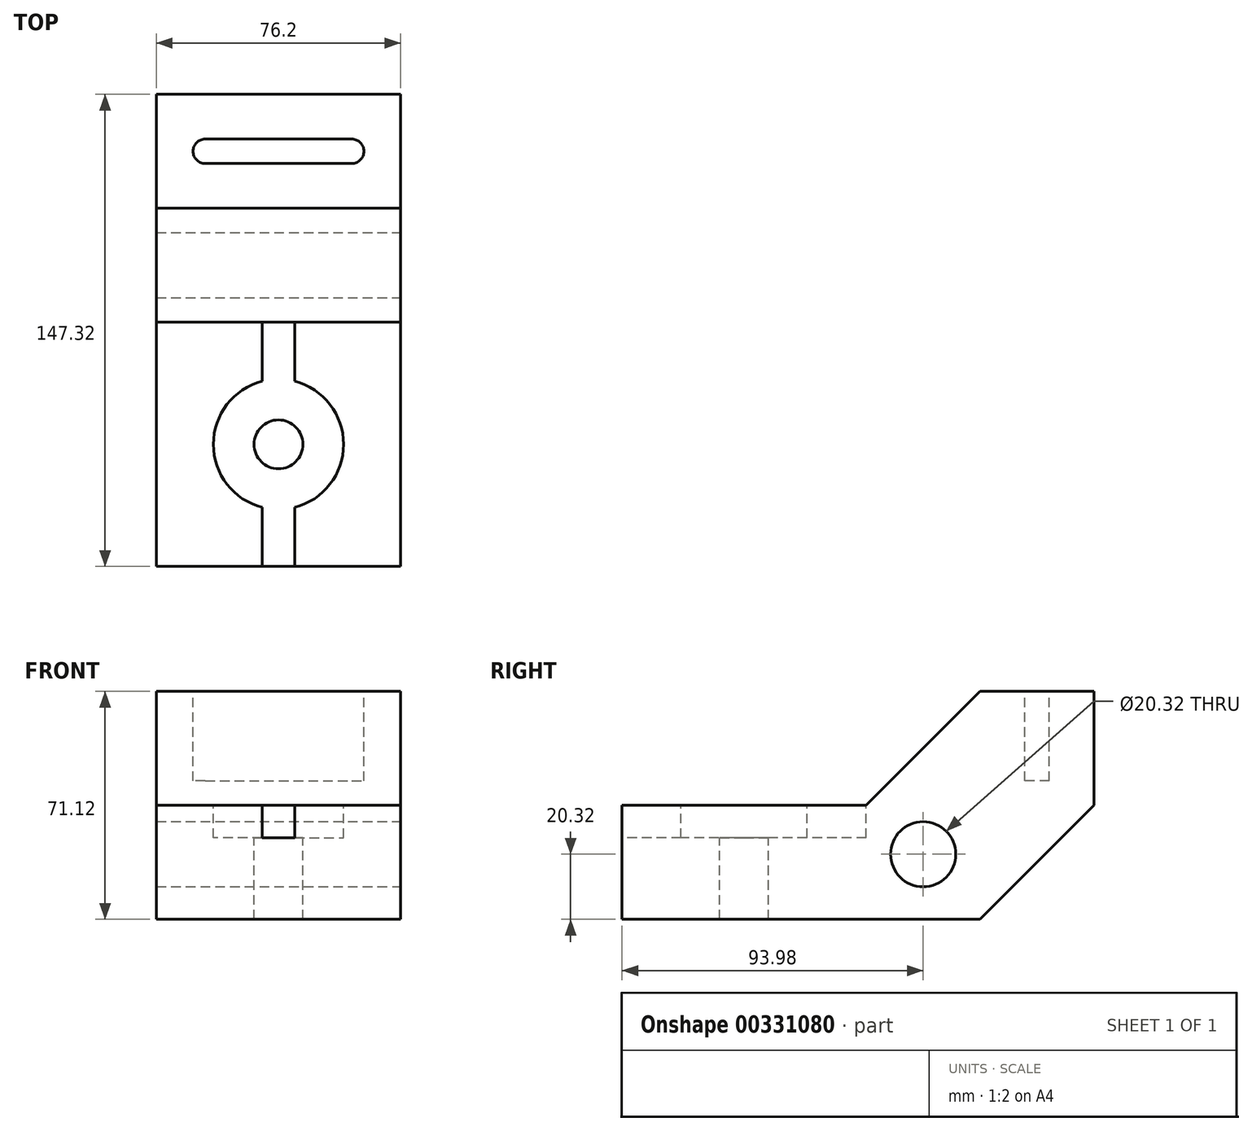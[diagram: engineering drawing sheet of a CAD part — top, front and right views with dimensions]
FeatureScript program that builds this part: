
annotation { "Feature Type Name" : "Feature", "Feature Type Description" : "" }
export const myFeature = defineFeature(function(context is Context, id is Id, definition is map)
    precondition{}
    {
        {
            var Q0;
            Q0=qCreatedBy(makeId("Right.planeOp"),FACE);
            var sketch = newSketch(context, id + "F0", { "sketchPlane" : qUnion([Q0])});
            skLineSegment(sketch, "E0.bottom", {"start": v(-73.66, 0) * mm, "end": v(73.66, 0) * mm});
            skLineSegment(sketch, "E0.top", {"start": v(-73.66, 71.12) * mm, "end": v(73.66, 71.12) * mm});
            skLineSegment(sketch, "E0.left", {"start": v(-73.66, 0) * mm, "end": v(-73.66, 71.12) * mm});
            skLineSegment(sketch, "E0.right", {"start": v(73.66, 0) * mm, "end": v(73.66, 71.12) * mm});
            skSolve(sketch);
        }
        {
            var Q0;
            Q0 = qSketchRegion(id + "F0", true);
            extrude(context, id + "F1", {"entities" : qUnion([Q0]), "endBound" : BoundingType.SYMMETRIC, "depth" : 76.2 * mm});
        }
        {
            var Q0;
            Q0=makeQuery(id+"F1.opExtrude","CAP_FACE",FACE,{"disambiguationData":[OSD([sQuery(id+"F0.wireOp",EDGE,"E0.bottom"),sQuery(id+"F0.wireOp",EDGE,"E0.top"),sQuery(id+"F0.wireOp",EDGE,"E0.left"),sQuery(id+"F0.wireOp",EDGE,"E0.right")])],"isStart":false});
            var sketch = newSketch(context, id + "F2", { "sketchPlane" : qUnion([Q0])});
            skLineSegment(sketch, "E1.0.0", {"start": v(38.1, 71.12) * mm, "end": v(-73.66, 71.12) * mm});
            skLineSegment(sketch, "E1.0.1", {"start": v(-73.66, 71.12) * mm, "end": v(-73.66, 35.56) * mm});
            skLineSegment(sketch, "E1.0.2", {"start": v(38.1, 0) * mm, "end": v(73.66, 0) * mm});
            skLineSegment(sketch, "E1.0.3", {"start": v(73.66, 0) * mm, "end": v(73.66, 35.56) * mm});
            skLineSegment(sketch, "E2", {"start": v(73.66, 35.56) * mm, "end": v(38.1, 0) * mm});
            skLineSegment(sketch, "E3", {"start": v(-73.66, 35.56) * mm, "end": v(2.54, 35.56) * mm});
            skLineSegment(sketch, "E4", {"start": v(2.54, 35.56) * mm, "end": v(38.1, 71.12) * mm});
            skPoint(sketch, "E5.orphan", {"position": v(-73.66, 0) * mm});
            skPoint(sketch, "E6.end.orphan", {"position": v(73.66, 71.12) * mm});
            skSolve(sketch);
        }
        {
            var Q0;
            Q0 = qSketchRegion(id + "F2", true);
            extrude(context, id + "F3", {"entities" : qUnion([Q0]), "operationType" : NewBodyOperationType.REMOVE, "endBound" : BoundingType.THROUGH_ALL, "oppositeDirection" : true, "depth" : 25.4 * mm});
        }
        {
            var Q0;
            Q0=makeQuery(id+"F1.opExtrude","CAP_FACE",FACE,{"disambiguationData":[OSD([sQuery(id+"F0.wireOp",EDGE,"E0.bottom"),sQuery(id+"F0.wireOp",EDGE,"E0.top"),sQuery(id+"F0.wireOp",EDGE,"E0.left"),sQuery(id+"F0.wireOp",EDGE,"E0.right")])],"isStart":false});
            var sketch = newSketch(context, id + "F4", { "sketchPlane" : qUnion([Q0])});
            skLineSegment(sketch, "E7.0.2", {"start": v(-73.66, 0) * mm, "end": v(38.1, 0) * mm});
            skLineSegment(sketch, "E7.0.4", {"start": v(73.66, 35.56) * mm, "end": v(73.66, 71.12) * mm});
            skCircle(sketch, "E8", {"center": v(20.32, 20.32) * mm, "radius": 10.16 * mm});
            skPoint(sketch, "E7.0.1.start.orphan", {"position": v(-73.66, 35.56) * mm});
            skPoint(sketch, "E7.0.6.end.orphan", {"position": v(2.54, 35.56) * mm});
            skPoint(sketch, "E7.0.5.end.orphan", {"position": v(38.1, 71.12) * mm});
            skSolve(sketch);
        }
        {
            var Q0;
            Q0=makeQuery(id+"F4.imprint","IMPRINT",FACE,{"disambiguationData":[TD([[makeQuery(id+"F4.imprint","IMPRINT",EDGE,{"derivedFrom":sQuery(id+"F4.wireOp",EDGE,"E8")}),1.0]])]});
            extrude(context, id + "F5", {"entities" : qUnion([Q0]), "operationType" : NewBodyOperationType.REMOVE, "endBound" : BoundingType.THROUGH_ALL, "oppositeDirection" : true, "depth" : 25.4 * mm});
        }
        {
            var Q0;
            Q0=makeQuery(id+"F3.boolean.opBoolean","COPY",FACE,{"derivedFrom":makeQuery(id+"F3.opExtrude","SWEPT_FACE",FACE,{"disambiguationData":[OSD([sQuery(id+"F2.wireOp",EDGE,"E3")])]})});
            var sketch = newSketch(context, id + "F6", { "sketchPlane" : qUnion([Q0])});
            skLineSegment(sketch, "E9.bottom", {"start": v(-5.08, 2.54) * mm, "end": v(5.08, 2.54) * mm});
            skLineSegment(sketch, "E9.top", {"start": v(-5.08, -73.66) * mm, "end": v(5.08, -73.66) * mm});
            skLineSegment(sketch, "E9.left", {"start": v(-5.08, 2.54) * mm, "end": v(-5.08, -73.66) * mm});
            skLineSegment(sketch, "E9.right", {"start": v(5.08, 2.54) * mm, "end": v(5.08, -73.66) * mm});
            skPoint(sketch, "E10", {"position": v(0, -35.56) * mm});
            skSolve(sketch);
        }
        {
            var Q0;
            Q0=makeQuery(id+"F6.imprint","IMPRINT",FACE,{"disambiguationData":[TD([[makeQuery(id+"F6.imprint","IMPRINT",EDGE,{"derivedFrom":sQuery(id+"F6.wireOp",EDGE,"E9.bottom")}),-1.0]])]});
            extrude(context, id + "F7", {"entities" : qUnion([Q0]), "operationType" : NewBodyOperationType.REMOVE, "oppositeDirection" : true, "depth" : 10.16 * mm});
        }
        {
            var Q0;
            Q0=sQuery(id+"F6.wireOp",VERTEX,"E10");
            var Q1;
            Q1=makeQuery(id+"F1.opExtrude","SWEPT_BODY",BODY,{"disambiguationData":[OSD([sQuery(id+"F0.wireOp",EDGE,"E0.bottom"),sQuery(id+"F0.wireOp",EDGE,"E0.top"),sQuery(id+"F0.wireOp",EDGE,"E0.left"),sQuery(id+"F0.wireOp",EDGE,"E0.right")])]});
            hole(context, id + "F8", {"style" : HoleStyle.C_BORE, "endStyle" : HoleEndStyle.THROUGH, "holeDiameter" : 15.24 * mm, "cBoreDiameter" : 40.64 * mm, "cBoreDepth" : 10.16 * mm, "tappedDepth" : 12.7 * mm, "tapClearance" : 3, "startFromSketch" : true, "locations" : qUnion([Q0]), "scope" : qUnion([Q1])});
        }
        {
            var Q0;
            Q0=makeQuery(id+"F1.opExtrude","SWEPT_FACE",FACE,{"disambiguationData":[OSD([sQuery(id+"F0.wireOp",EDGE,"E0.top")])]});
            var sketch = newSketch(context, id + "F9", { "sketchPlane" : qUnion([Q0])});
            skArc(sketch, "E11", {"start": v(-22.86, 59.7) * mm, "mid": v(-26.67, 55.88) * mm, "end": v(-22.86, 52.07) * mm});
            skArc(sketch, "E12", {"start": v(22.86, 52.07) * mm, "mid": v(26.67, 55.88) * mm, "end": v(22.86, 59.7) * mm});
            skLineSegment(sketch, "E13", {"start": v(-22.86, 59.7) * mm, "end": v(22.86, 59.7) * mm});
            skLineSegment(sketch, "E14", {"start": v(22.86, 52.07) * mm, "end": v(-22.86, 52.07) * mm});
            skSolve(sketch);
        }
        {
            var Q0;
            Q0 = qSketchRegion(id + "F9", true);
            extrude(context, id + "F10", {"entities" : qUnion([Q0]), "operationType" : NewBodyOperationType.REMOVE, "oppositeDirection" : true, "depth" : 27.94 * mm});
        }
    });
